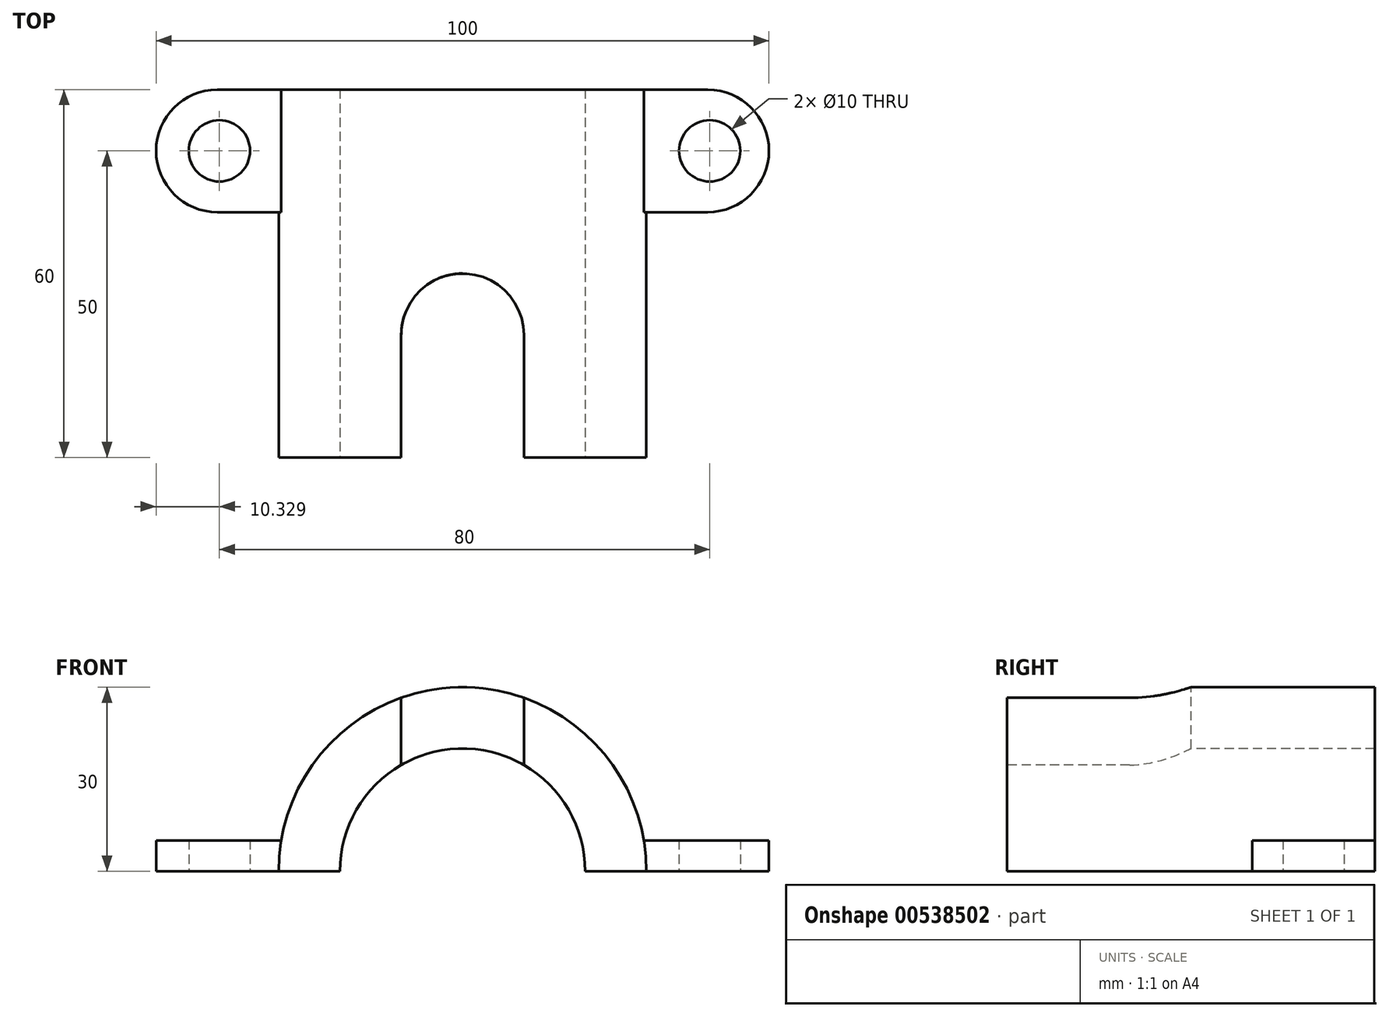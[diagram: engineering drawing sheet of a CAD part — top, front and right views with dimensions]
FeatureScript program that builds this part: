
annotation { "Feature Type Name" : "Feature", "Feature Type Description" : "" }
export const myFeature = defineFeature(function(context is Context, id is Id, definition is map)
    precondition{}
    {
        {
            var Q0;
            Q0=qCreatedBy(makeId("Front.planeOp"),FACE);
            var sketch = newSketch(context, id + "F0", { "sketchPlane" : qUnion([Q0])});
            skCircle(sketch, "E0", {"center": v(0, 0) * mm, "radius": 30 * mm});
            skSolve(sketch);
        }
        {
            var Q0;
            Q0 = qSketchRegion(id + "F0", true);
            extrude(context, id + "F1", {"entities" : qUnion([Q0]), "depth" : 60 * mm, "offsetDistance" : 25 * mm});
        }
        {
            var Q0;
            Q0=makeQuery(id+"F1.opExtrude","CAP_FACE",FACE,{"disambiguationData":[OSD([sQuery(id+"F0.wireOp",EDGE,"E0")])],"isStart":false});
            var sketch = newSketch(context, id + "F2", { "sketchPlane" : qUnion([Q0])});
            skLineSegment(sketch, "E1", {"start": v(-30, 0) * mm, "end": v(30, 0) * mm});
            skSolve(sketch);
        }
        {
            var Q0;
            {var subQ0=sQuery(id+"F2.wireOp",EDGE,"E1");Q0=makeQuery(id+"F2.imprint","IMPRINT",FACE,{"disambiguationData":[TD([[makeQuery(id+"F2.imprint","IMPRINT",EDGE,{"derivedFrom":subQ0}),-1.0]])]});}
            extrude(context, id + "F3", {"entities" : qUnion([Q0]), "operationType" : NewBodyOperationType.REMOVE, "endBound" : BoundingType.UP_TO_NEXT, "oppositeDirection" : true, "depth" : 25 * mm, "offsetDistance" : 25 * mm});
        }
        {
            var Q0;
            Q0=qCreatedBy(makeId("Top.planeOp"),FACE);
            var sketch = newSketch(context, id + "F4", { "sketchPlane" : qUnion([Q0])});
            skLineSegment(sketch, "E2", {"start": v(-40, 0) * mm, "end": v(40, 0) * mm});
            skLineSegment(sketch, "E3", {"start": v(-39.67, -10) * mm, "end": v(40.33, -10) * mm, "construction": true});
            skLineSegment(sketch, "E4", {"start": v(-40, -20) * mm, "end": v(40, -20) * mm});
            skArc(sketch, "E5", {"start": v(40, -20) * mm, "mid": v(50, -10) * mm, "end": v(40, 0) * mm});
            skArc(sketch, "E6", {"start": v(-40, 0) * mm, "mid": v(-50, -10) * mm, "end": v(-40, -20) * mm});
            skCircle(sketch, "E7", {"center": v(-39.67, -10) * mm, "radius": 5 * mm});
            skCircle(sketch, "E8", {"center": v(40.33, -10) * mm, "radius": 5 * mm});
            skSolve(sketch);
        }
        {
            var Q0;
            Q0=makeQuery(id+"F4.imprint","IMPRINT",FACE,{"disambiguationData":[TD([[makeQuery(id+"F4.imprint","IMPRINT",EDGE,{"derivedFrom":sQuery(id+"F4.wireOp",EDGE,"E2")}),-1.0]])]});
            extrude(context, id + "F5", {"entities" : qUnion([Q0]), "operationType" : NewBodyOperationType.ADD, "depth" : 5 * mm, "offsetDistance" : 25 * mm});
        }
        {
            var Q0;
            Q0=makeQuery(id+"F1.opExtrude","CAP_FACE",FACE,{"disambiguationData":[OSD([sQuery(id+"F0.wireOp",EDGE,"E0")])],"isStart":false});
            var sketch = newSketch(context, id + "F6", { "sketchPlane" : qUnion([Q0])});
            skCircle(sketch, "E9", {"center": v(0, 0) * mm, "radius": 20 * mm});
            skSolve(sketch);
        }
        {
            var Q0;
            {var subQ0=sQuery(id+"F6.wireOp",EDGE,"E9");var subQ1=makeQuery(id+"F3.boolean.opBoolean","COPY",EDGE,{"derivedFrom":makeQuery(id+"F3.opExtrude","CAP_EDGE",EDGE,{"disambiguationData":[OSD([sQuery(id+"F2.wireOp",EDGE,"E1")])],"isStart":true})});var subQ2=makeQuery(id+"F6.imprint","INTERSECT",VERTEX,{"disambiguationData":[OD(0.0)],"derivedFrom":[subQ1,subQ0]});Q0=makeQuery(id+"F6.imprint","IMPRINT",FACE,{"disambiguationData":[TD([[makeQuery(id+"F6.imprint","IMPRINT",EDGE,{"disambiguationData":[TD([[subQ2,1.0]])],"derivedFrom":subQ0}),1.0]])]});}
            extrude(context, id + "F7", {"entities" : qUnion([Q0]), "operationType" : NewBodyOperationType.REMOVE, "endBound" : BoundingType.UP_TO_NEXT, "oppositeDirection" : true, "depth" : 25 * mm, "offsetDistance" : 25 * mm});
        }
        {
            var Q0;
            Q0=makeQuery(id+"F1.opExtrude","CAP_EDGE",EDGE,{"disambiguationData":[OSD([sQuery(id+"F0.wireOp",EDGE,"E0")])],"isStart":false});
            cPoint(context, id + "F8", {"entities" : qUnion([Q0]), "parameter" : 0.5});
        }
        {
            var Q0;
            Q0=qCreatedBy(makeId("Top.planeOp"),FACE);
            var Q1;
            Q1 = qCreatedBy(id + "F8" ,VERTEX);
            cPlane(context, id + "F9", {"entities" : qUnion([Q0, Q1]), "cplaneType" : CPlaneType.PLANE_POINT, "offset" : 25 * mm, "width" : 150 * mm, "height" : 150 * mm});
        }
        {
            var Q0;
            Q0=qCreatedBy(id+"F9.planeOp",FACE);
            var sketch = newSketch(context, id + "F10", { "sketchPlane" : qUnion([Q0])});
            skLineSegment(sketch, "E10.bottom", {"start": v(10, -40) * mm, "end": v(-10, -40) * mm});
            skLineSegment(sketch, "E10.top", {"start": v(10, -80) * mm, "end": v(-10, -80) * mm});
            skLineSegment(sketch, "E10.left", {"start": v(10, -40) * mm, "end": v(10, -80) * mm});
            skLineSegment(sketch, "E10.right", {"start": v(-10, -40) * mm, "end": v(-10, -80) * mm});
            skPoint(sketch, "E10.middle", {"position": v(0, -60) * mm});
            skArc(sketch, "E11", {"start": v(10, -40) * mm, "mid": v(0, -30) * mm, "end": v(-10, -40) * mm});
            skSolve(sketch);
        }
        {
            var Q0;
            Q0=makeQuery(id+"F10.imprint","IMPRINT",FACE,{"disambiguationData":[TD([[makeQuery(id+"F10.imprint","IMPRINT",EDGE,{"derivedFrom":sQuery(id+"F10.wireOp",EDGE,"E10.bottom")}),-1.0]])]});
            var Q1;
            Q1=makeQuery(id+"F10.imprint","IMPRINT",FACE,{"disambiguationData":[TD([[makeQuery(id+"F10.imprint","IMPRINT",EDGE,{"derivedFrom":sQuery(id+"F10.wireOp",EDGE,"E10.bottom")}),1.0]])]});
            extrude(context, id + "F11", {"entities" : qUnion([Q0, Q1]), "operationType" : NewBodyOperationType.REMOVE, "oppositeDirection" : true, "depth" : 25 * mm, "offsetDistance" : 25 * mm});
        }
    });
